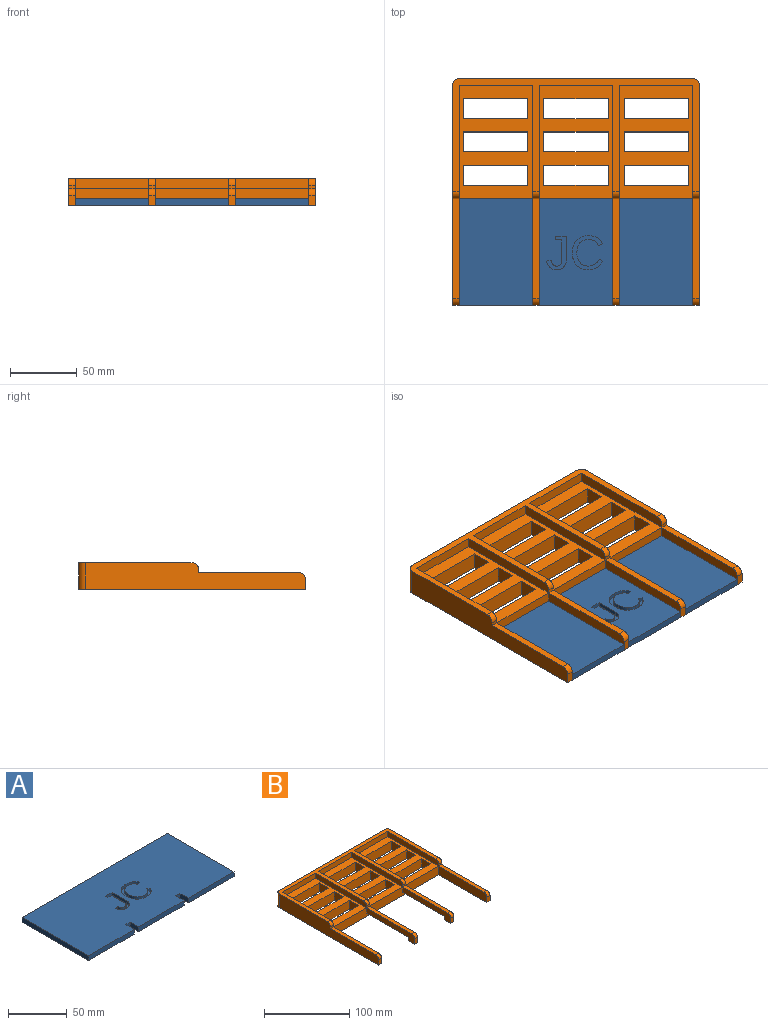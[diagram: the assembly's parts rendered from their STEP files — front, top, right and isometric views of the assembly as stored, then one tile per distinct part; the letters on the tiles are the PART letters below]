
ASSEMBLY  parts=2 mates=1
PART A: 47 faces, bbox 175x80x5 mm
  f0: plane 175x80mm, normal (0,0,1), area 13595.1mm2, adj f1,f2,f3,f4,f5,f6,f7,f8
  f1: plane 10x5mm, normal (1,0,0), area 50mm2, adj f0,f2,f12,f13
  f2: plane 5x5mm, normal (0,-1,0), area 25mm2, adj f0,f1,f3,f13
  f3: plane 10x5mm, normal (-1,0,0), area 50mm2, adj f0,f2,f4,f13
  f4: plane 55x5mm, normal (0,-1,0), area 275mm2, adj f0,f3,f5,f13
  f5: plane 10x5mm, normal (1,0,0), area 50mm2, adj f0,f4,f6,f13
  f6: plane 5x5mm, normal (0,-1,0), area 25mm2, adj f0,f5,f7,f13
  f7: plane 10x5mm, normal (-1,0,0), area 50mm2, adj f0,f6,f8,f13
  f8: plane 55x5mm, normal (0,-1,0), area 275mm2, adj f0,f7,f9,f13
  f9: plane 80x5mm, normal (1,0,0), area 400mm2, adj f0,f8,f10,f13
  f10: plane 175x5mm, normal (0,1,0), area 875mm2, adj f0,f9,f11,f13
  f11: plane 80x5mm, normal (-1,0,0), area 400mm2, adj f0,f10,f12,f13
  f12: plane 55x5mm, normal (0,-1,0), area 275mm2, adj f0,f1,f11,f13
  f13: plane 175x80mm, normal (0,0,-1), area 13900mm2, adj f1,f2,f3,f4,f5,f6,f7,f8
  f14: extruded ~6.38x3mm, area 21.4mm2, adj f0,f15,f31,f32
  f15: extruded ~4.52x3mm, area 14.1mm2, adj f0,f14,f16,f32
  f16: extruded ~3.29x3mm, area 13.1mm2, adj f0,f15,f17,f32
  f17: plane 3.18x3mm, normal (-0.31,0.95,0), area 10mm2, adj f0,f16,f18,f32
  f18: extruded ~4.58x3.89mm, area 18.4mm2, adj f0,f17,f19,f32
  f19: extruded ~6.59x3mm, area 20.5mm2, adj f0,f18,f20,f32
  f20: extruded ~8.84x3.35mm, area 29.2mm2, adj f0,f19,f21,f32
  f21: extruded ~9.26x3.19mm, area 30.1mm2, adj f0,f20,f22,f32
  f22: extruded ~6.83x3mm, area 21.1mm2, adj f0,f21,f23,f32
  f23: extruded ~4.44x4.15mm, area 18.5mm2, adj f0,f22,f24,f32
  f24: extruded ~6.46x3mm, area 20.2mm2, adj f0,f23,f25,f32
  f25: extruded ~6.41x3mm, area 20.1mm2, adj f0,f24,f26,f32
  f26: extruded ~4.86x4.29mm, area 19.7mm2, adj f0,f25,f27,f32
  f27: plane 3x2.73mm, normal (-0.45,-0.89,0), area 9.2mm2, adj f0,f26,f28,f32
  f28: extruded ~7.8x5.14mm, area 29.7mm2, adj f0,f27,f29,f32
  f29: extruded ~6.43x3mm, area 21.7mm2, adj f0,f28,f30,f32
  f30: extruded ~7.3x3mm, area 23.5mm2, adj f0,f29,f31,f32
  f31: extruded ~7.23x3mm, area 23.2mm2, adj f0,f14,f30,f32
  f32: plane 25.42x22.74mm, normal (0,0,1), area 177.5mm2, adj f14,f15,f16,f17,f18,f19,f20,f21
  f33: extruded ~7.45x6.49mm, area 32.8mm2, adj f0,f34,f45,f46
  f34: extruded ~5.33x3mm, area 17.7mm2, adj f0,f33,f35,f46
  f35: extruded ~5.66x3mm, area 18.4mm2, adj f0,f34,f36,f46
  f36: plane 17.33x3mm, normal (-1,0,0), area 52mm2, adj f0,f35,f37,f46
  f37: plane 8.08x3mm, normal (0,-1,0), area 24.3mm2, adj f0,f36,f38,f46
  f38: plane 3x2.73mm, normal (1,0,0), area 8.2mm2, adj f0,f37,f39,f46
  f39: plane 4.75x3mm, normal (0,1,0), area 14.3mm2, adj f0,f38,f40,f46
  f40: plane 14.67x3mm, normal (1,0,0), area 44mm2, adj f0,f39,f41,f46
  f41: extruded ~3.67x3mm, area 11.7mm2, adj f0,f40,f42,f46
  f42: extruded ~3x2.88mm, area 9.7mm2, adj f0,f41,f43,f46
  f43: extruded ~3x2.77mm, area 9.2mm2, adj f0,f42,f44,f46
  f44: extruded ~3.18x3mm, area 10.6mm2, adj f0,f43,f45,f46
  f45: plane 3.28x3mm, normal (0.16,-0.99,0), area 10mm2, adj f0,f33,f44,f46
  f46: plane 25.05x14.73mm, normal (0,0,1), area 127.4mm2, adj f33,f34,f35,f36,f37,f38,f39,f40
PART B: 88 faces, bbox 185x170x20 mm
  f0: plane 85x55mm, normal (0,0,1), area 2515mm2, adj f4,f17,f18,f19,f56,f57,f58,f59
  f1: plane 85x55mm, normal (0,0,1), area 2515mm2, adj f4,f23,f24,f25,f52,f53,f54,f55
  f2: plane 85x55mm, normal (0,0,1), area 2515mm2, adj f4,f20,f21,f22,f60,f61,f62,f63
  f3: plane 185x170mm, normal (0,0,-1), area 10959.3mm2, adj f4,f14,f15,f16,f27,f28,f30,f31
  f4: plane 175x12.5mm, normal (0,-1,0), area 2112.5mm2, adj f0,f1,f2,f3,f7,f8,f28,f30
  f5: plane 5x5mm, normal (0,1,0), area 25mm2, adj f7,f8,f10,f50
  f6: plane 7.5x5mm, normal (0,-1,0), area 37.5mm2, adj f7,f8,f10,f11
  f7: plane 80x12.5mm, normal (1,0,0), area 644.6mm2, adj f4,f5,f6,f9,f10,f11,f50
  f8: plane 80x12.5mm, normal (-1,0,0), area 644.6mm2, adj f4,f5,f6,f9,f10,f11,f50
  f9: plane 75x5mm, normal (0,0,1), area 375mm2, adj f7,f8,f11,f12
  f10: plane 10x5mm, normal (0,0,-1), area 50mm2, adj f5,f6,f7,f8
  f11: cylinder r=5mm len=5mm, axis (-1,0,0), area 39.3mm2, adj f6,f7,f8,f9
  f12: plane 5x2.5mm, normal (0,-1,0), area 12.5mm2, adj f9,f22,f23,f45
  f13: plane 75x5mm, normal (0,0,1), area 375mm2, adj f14,f30,f32,f46
  f14: plane 165x20mm, normal (1,0,0), area 2689.3mm2, adj f3,f13,f26,f31,f32,f34,f46,f47
  f15: plane 175x20mm, normal (0,1,0), area 3500mm2, adj f3,f26,f34,f35
  f16: plane 165x20mm, normal (-1,0,0), area 2689.3mm2, adj f3,f26,f27,f29,f33,f35,f48,f49
  f17: plane 85x7.5mm, normal (1,0,0), area 632.1mm2, adj f0,f18,f26,f48,f49
  f18: plane 55x7.5mm, normal (0,-1,0), area 412.5mm2, adj f0,f17,f19,f26
  f19: plane 85x7.5mm, normal (-1,0,0), area 632.1mm2, adj f0,f18,f26,f38,f39
  f20: plane 85x7.5mm, normal (1,0,0), area 632.1mm2, adj f2,f21,f26,f38,f39
  f21: plane 55x7.5mm, normal (0,-1,0), area 412.5mm2, adj f2,f20,f22,f26
  f22: plane 85x7.5mm, normal (-1,0,0), area 632.1mm2, adj f2,f12,f21,f26,f45
  f23: plane 85x7.5mm, normal (1,0,0), area 632.1mm2, adj f1,f12,f24,f26,f45
  f24: plane 55x7.5mm, normal (0,-1,0), area 412.5mm2, adj f1,f23,f25,f26
  f25: plane 85x7.5mm, normal (-1,0,0), area 632.1mm2, adj f1,f24,f26,f46,f47
  f26: plane 185x85mm, normal (0,0,1), area 2514.3mm2, adj f14,f15,f16,f17,f18,f19,f20,f21
  f27: plane 7.5x5mm, normal (0,-1,0), area 37.5mm2, adj f3,f16,f28,f33
  f28: plane 80x12.5mm, normal (1,0,0), area 994.6mm2, adj f3,f4,f27,f29,f33
  f29: plane 75x5mm, normal (0,0,1), area 375mm2, adj f16,f28,f33,f48
  f30: plane 80x12.5mm, normal (-1,0,0), area 994.6mm2, adj f3,f4,f13,f31,f32
  f31: plane 7.5x5mm, normal (0,-1,0), area 37.5mm2, adj f3,f14,f30,f32
  f32: cylinder r=5mm len=5mm, axis (-1,0,0), area 39.3mm2, adj f13,f14,f30,f31
  f33: cylinder r=5mm len=5mm, axis (-1,0,0), area 39.3mm2, adj f16,f27,f28,f29
  f34: cylinder r=5mm len=20mm, axis (0,0,1), area 157.1mm2, adj f3,f14,f15,f26
  f35: cylinder r=5mm len=20mm, axis (0,0,-1), area 157.1mm2, adj f3,f15,f16,f26
  f36: plane 80x12.5mm, normal (-1,0,0), area 644.6mm2, adj f4,f40,f41,f42,f43,f44,f51
  f37: plane 80x12.5mm, normal (1,0,0), area 644.6mm2, adj f4,f40,f41,f42,f43,f44,f51
  f38: plane 5x2.5mm, normal (0,-1,0), area 12.5mm2, adj f19,f20,f39,f42
  f39: cylinder r=5mm len=5mm, axis (-1,0,0), area 39.3mm2, adj f19,f20,f26,f38
  f40: plane 7.5x5mm, normal (0,-1,0), area 37.5mm2, adj f36,f37,f43,f44
  f41: plane 5x5mm, normal (0,1,0), area 25mm2, adj f36,f37,f43,f51
  f42: plane 75x5mm, normal (0,0,1), area 375mm2, adj f36,f37,f38,f44
  f43: plane 10x5mm, normal (0,0,-1), area 50mm2, adj f36,f37,f40,f41
  f44: cylinder r=5mm len=5mm, axis (-1,0,0), area 39.3mm2, adj f36,f37,f40,f42
  f45: cylinder r=5mm len=5mm, axis (-1,0,0), area 39.3mm2, adj f12,f22,f23,f26
  f46: plane 5x2.5mm, normal (0,-1,0), area 12.5mm2, adj f13,f14,f25,f47
  f47: cylinder r=5mm len=5mm, axis (-1,0,0), area 39.3mm2, adj f14,f25,f26,f46
  f48: plane 5x2.5mm, normal (0,-1,0), area 12.5mm2, adj f16,f17,f29,f49
  f49: cylinder r=5mm len=5mm, axis (-1,0,0), area 39.3mm2, adj f16,f17,f26,f48
  f50: plane 70x5mm, normal (0,0,-1), area 350mm2, adj f4,f5,f7,f8
  f51: plane 70x5mm, normal (0,0,-1), area 350mm2, adj f4,f36,f37,f41
  f52: plane 15x12.5mm, normal (-1,0,0), area 187.5mm2, adj f1,f3,f53,f55
  f53: plane 48x12.5mm, normal (0,-1,0), area 600mm2, adj f1,f3,f52,f54
  f54: plane 15x12.5mm, normal (1,0,0), area 187.5mm2, adj f1,f3,f53,f55
  f55: plane 48x12.5mm, normal (0,1,0), area 600mm2, adj f1,f3,f52,f54
  f56: plane 15x12.5mm, normal (1,0,0), area 187.5mm2, adj f0,f3,f57,f59
  f57: plane 48x12.5mm, normal (0,1,0), area 600mm2, adj f0,f3,f56,f58
  f58: plane 15x12.5mm, normal (-1,0,0), area 187.5mm2, adj f0,f3,f57,f59
  f59: plane 48x12.5mm, normal (0,-1,0), area 600mm2, adj f0,f3,f56,f58
  f60: plane 48x12.5mm, normal (0,1,0), area 600mm2, adj f2,f3,f61,f63
  f61: plane 15x12.5mm, normal (-1,0,0), area 187.5mm2, adj f2,f3,f60,f62
  f62: plane 48x12.5mm, normal (0,-1,0), area 600mm2, adj f2,f3,f61,f63
  f63: plane 15x12.5mm, normal (1,0,0), area 187.5mm2, adj f2,f3,f60,f62
  f64: plane 15x12.5mm, normal (-1,0,0), area 187.5mm2, adj f2,f3,f65,f67
  f65: plane 48x12.5mm, normal (0,-1,0), area 600mm2, adj f2,f3,f64,f66
  f66: plane 15x12.5mm, normal (1,0,0), area 187.5mm2, adj f2,f3,f65,f67
  f67: plane 48x12.5mm, normal (0,1,0), area 600mm2, adj f2,f3,f64,f66
  f68: plane 15x12.5mm, normal (-1,0,0), area 187.5mm2, adj f2,f3,f69,f71
  f69: plane 48x12.5mm, normal (0,-1,0), area 600mm2, adj f2,f3,f68,f70
  f70: plane 15x12.5mm, normal (1,0,0), area 187.5mm2, adj f2,f3,f69,f71
  f71: plane 48x12.5mm, normal (0,1,0), area 600mm2, adj f2,f3,f68,f70
  f72: plane 15x12.5mm, normal (1,0,0), area 187.5mm2, adj f0,f3,f73,f75
  f73: plane 48x12.5mm, normal (0,1,0), area 600mm2, adj f0,f3,f72,f74
  f74: plane 15x12.5mm, normal (-1,0,0), area 187.5mm2, adj f0,f3,f73,f75
  f75: plane 48x12.5mm, normal (0,-1,0), area 600mm2, adj f0,f3,f72,f74
  f76: plane 48x12.5mm, normal (0,1,0), area 600mm2, adj f0,f3,f77,f79
  f77: plane 15x12.5mm, normal (-1,0,0), area 187.5mm2, adj f0,f3,f76,f78
  f78: plane 48x12.5mm, normal (0,-1,0), area 600mm2, adj f0,f3,f77,f79
  f79: plane 15x12.5mm, normal (1,0,0), area 187.5mm2, adj f0,f3,f76,f78
  f80: plane 15x12.5mm, normal (-1,0,0), area 187.5mm2, adj f1,f3,f81,f83
  f81: plane 48x12.5mm, normal (0,-1,0), area 600mm2, adj f1,f3,f80,f82
  f82: plane 15x12.5mm, normal (1,0,0), area 187.5mm2, adj f1,f3,f81,f83
  f83: plane 48x12.5mm, normal (0,1,0), area 600mm2, adj f1,f3,f80,f82
  f84: plane 15x12.5mm, normal (-1,0,0), area 187.5mm2, adj f1,f3,f85,f87
  f85: plane 48x12.5mm, normal (0,-1,0), area 600mm2, adj f1,f3,f84,f86
  f86: plane 15x12.5mm, normal (1,0,0), area 187.5mm2, adj f1,f3,f85,f87
  f87: plane 48x12.5mm, normal (0,1,0), area 600mm2, adj f1,f3,f84,f86
PLACE A t=(30,0,5)mm
PLACE B at identity
MATE fastened B.f43 <-> A.f13  axis (0,0,-1) through (60,-35,5)mm
